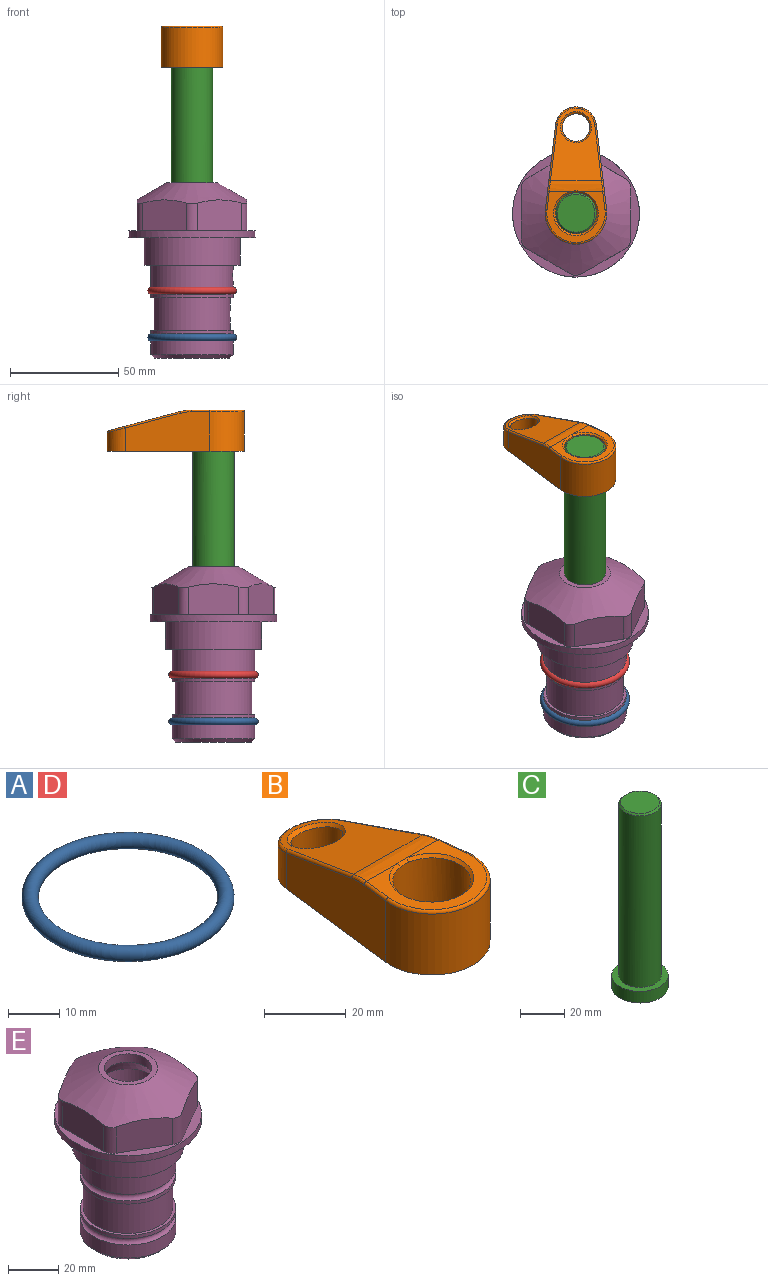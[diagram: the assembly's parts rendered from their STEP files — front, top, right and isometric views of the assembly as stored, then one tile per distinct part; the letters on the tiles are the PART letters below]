
ASSEMBLY  parts=5 mates=4
PART A: 1 faces, bbox 44.7x44.7x3.2 mm
  f0: torus R=19.05mm, axis (0,0,1), area 1193.9mm2
PART B: 31 faces, bbox 31.7x65.5x19.8 mm
  f0: plane 39.12x18.26mm, normal (0.99,0.12,0), area 612.2mm2, adj f1,f4,f7,f11,f13,f15
  f1: cylinder r=9.53mm len=18.91mm, axis (0,0,-1), area 296.1mm2, adj f0,f2,f7,f17
  f2: plane 39.12x18.26mm, normal (-0.99,0.12,0), area 612.2mm2, adj f1,f4,f7,f12,f14,f16
  f3: cylinder r=6.35mm len=12.7mm, axis (0,0,-1), area 362.4mm2, adj f7,f18
  f4: cylinder r=14.29mm len=28.58mm, axis (0,0,-1), area 882.2mm2, adj f0,f2,f7,f10
  f5: cylinder r=9.53mm len=19.05mm, axis (0,0,-1), area 1092.6mm2, adj f7,f19,f20
  f6: plane 26.99x23.69mm, normal (0,0,1), area 216.2mm2, adj f9,f10,f11,f12,f19
  f7: plane 63.5x28.58mm, normal (0,0,-1), area 661.8mm2, adj f0,f1,f2,f3,f4,f5,f22,f23
  f8: plane 33.52x23.6mm, normal (0,0.26,0.97), area 486mm2, adj f9,f15,f16,f17,f18
  f9: cylinder r=19.05mm len=24.72mm, axis (1,0,0), area 120.4mm2, adj f6,f8,f13,f14,f20
  f10: torus R=13.49mm, axis (0,0,1), area 59mm2, adj f4,f6,f11,f12
  f11: cylinder r=0.79mm len=8.67mm, axis (0.12,-0.99,0), area 10.8mm2, adj f0,f6,f10,f13
  f12: cylinder r=0.79mm len=8.67mm, axis (0.12,0.99,0), area 10.8mm2, adj f2,f6,f10,f14
  f13: bspline ~4.95x1.42mm, area 6.1mm2, adj f0,f9,f11,f15
  f14: bspline ~4.95x1.42mm, area 6.1mm2, adj f2,f9,f12,f16
  f15: cylinder r=0.79mm len=25.95mm, axis (0.12,-0.96,0.26), area 32.9mm2, adj f0,f8,f13,f17
  f16: cylinder r=0.79mm len=25.95mm, axis (0.12,0.96,-0.26), area 32.9mm2, adj f2,f8,f14,f17
  f17: bspline ~18.91x8.38mm, area 30mm2, adj f1,f8,f15,f16
  f18: bspline ~14.29x14.29mm, area 48.3mm2, adj f3,f8
  f19: cone r=9.53mm half-angle=45deg, axis (0,0,1), area 66.5mm2, adj f5,f6,f20
  f20: bspline ~3.22x0.96mm, area 3.5mm2, adj f5,f9,f19
  f21: plane 2.75x2.72mm, normal (0,0,-1), area 2.9mm2, adj f23,f25,f28
  f22: plane 23.05x15.88mm, normal (-0.99,-0.12,0), area 323.6mm2, adj f7,f25,f26,f27,f28,f29
  f23: plane 23.05x15.88mm, normal (0.99,-0.12,0), area 323.6mm2, adj f7,f21,f25,f27,f28,f30
  f24: cylinder r=9.53mm len=10.69mm, axis (0,0,-1), area 114.7mm2, adj f7,f27,f29,f30
  f25: cylinder r=12.7mm len=20.59mm, axis (0,0,-1), area 381.1mm2, adj f7,f21,f22,f23,f26,f28
  f26: plane 2.75x2.72mm, normal (0,0,-1), area 2.9mm2, adj f22,f25,f28
  f27: plane 19.72x18.37mm, normal (0,-0.26,-0.97), area 291.8mm2, adj f22,f23,f24,f28,f29,f30
  f28: cylinder r=15.88mm len=19.92mm, axis (1,0,0), area 54.8mm2, adj f21,f22,f23,f25,f26,f27
  f29: cylinder r=1.59mm len=11mm, axis (0,0,-1), area 34.7mm2, adj f7,f22,f24,f27
  f30: cylinder r=1.59mm len=11mm, axis (0,0,-1), area 34.7mm2, adj f7,f23,f24,f27
PART C: 6 faces, bbox 25.4x25.4x101.6 mm
  f0: plane 17.46x17.46mm, normal (0,0,1), area 239.5mm2, adj f5
  f1: plane 25.4x25.4mm, normal (0,0,-1), area 506.7mm2, adj f2
  f2: cylinder r=12.7mm len=25.4mm, axis (0,0,1), area 506.7mm2, adj f1,f3
  f3: plane 25.4x25.4mm, normal (0,0,1), area 221.7mm2, adj f2,f4
  f4: cylinder r=9.53mm len=94.46mm, axis (0,0,1), area 5653mm2, adj f3,f5
  f5: cone r=8.73mm half-angle=45deg, axis (0,0,-1), area 64.4mm2, adj f0,f4
PART D: same geometry as A
PART E: 36 faces, bbox 58.7x58.7x81 mm
  f0: cylinder r=17.78mm len=35.56mm, axis (0,0,1), area 1670.8mm2, adj f23,f24,f31
  f1: cylinder r=19.05mm len=38.1mm, axis (0,0,1), area 1191.9mm2, adj f26,f27,f30
  f2: plane 58.66x58.66mm, normal (0,0,-1), area 1150.6mm2, adj f3,f28
  f3: cylinder r=29.33mm len=58.66mm, axis (0,0,-1), area 585.1mm2, adj f2,f4
  f4: plane 58.66x58.66mm, normal (0,0,1), area 475.9mm2, adj f3,f5,f6,f7,f8,f9,f10,f11
  f5: plane 20.32x14.34mm, normal (-0.5,0.87,0), area 324.4mm2, adj f4,f15,f16,f17
  f6: plane 20.32x14.34mm, normal (0.5,0.87,0), area 324.4mm2, adj f4,f14,f15,f17
  f7: plane 23.48x14.34mm, normal (1,0,0), area 324.4mm2, adj f4,f13,f14,f17
  f8: plane 20.32x14.34mm, normal (0.5,-0.87,0), area 324.4mm2, adj f4,f12,f13,f17
  f9: plane 20.32x14.34mm, normal (-0.5,-0.87,0), area 324.4mm2, adj f4,f11,f12,f17
  f10: plane 23.48x14.34mm, normal (-1,0,0), area 324.4mm2, adj f4,f11,f16,f17
  f11: cylinder r=5.08mm len=12.85mm, axis (0,0,-1), area 67.2mm2, adj f4,f9,f10,f17
  f12: cylinder r=5.08mm len=12.85mm, axis (0,0,-1), area 67.2mm2, adj f4,f8,f9,f17
  f13: cylinder r=5.08mm len=12.85mm, axis (0,0,-1), area 67.2mm2, adj f4,f7,f8,f17
  f14: cylinder r=5.08mm len=12.85mm, axis (0,0,-1), area 67.2mm2, adj f4,f6,f7,f17
  f15: cylinder r=5.08mm len=12.85mm, axis (0,0,-1), area 67.2mm2, adj f4,f5,f6,f17
  f16: cylinder r=5.08mm len=12.85mm, axis (0,0,-1), area 67.2mm2, adj f4,f5,f10,f17
  f17: cone r=11.73mm half-angle=60deg, axis (0,0,-1), area 2071.8mm2, adj f5,f6,f7,f8,f9,f10,f11,f12
  f18: plane 23.46x23.46mm, normal (0,0,1), area 147.4mm2, adj f17,f35
  f19: plane 34.93x34.93mm, normal (0,0,-1), area 958mm2, adj f29
  f20: cylinder r=19.05mm len=38.1mm, axis (0,0,1), area 760.1mm2, adj f21,f29
  f21: torus R=19.05mm, axis (0,0,1), area 565.3mm2, adj f20,f22
  f22: cylinder r=19.05mm len=38.1mm, axis (0,0,1), area 190mm2, adj f21,f23
  f23: plane 38.1x38.1mm, normal (0,0,1), area 146.9mm2, adj f0,f22
  f24: plane 38.1x38.1mm, normal (0,0,-1), area 146.9mm2, adj f0,f25
  f25: cylinder r=19.05mm len=38.1mm, axis (0,0,1), area 190mm2, adj f24,f26
  f26: torus R=19.05mm, axis (0,0,1), area 565.3mm2, adj f1,f25
  f27: plane 44.45x44.45mm, normal (0,0,-1), area 411.7mm2, adj f1,f28
  f28: cylinder r=22.23mm len=44.45mm, axis (0,0,1), area 1773.5mm2, adj f2,f27
  f29: cone r=19.05mm half-angle=45deg, axis (0,0,1), area 257.5mm2, adj f19,f20
  f30: cylinder r=3.17mm len=6.75mm, axis (-1,0,0), area 128mm2, adj f1,f33
  f31: cylinder r=3.17mm len=6.35mm, axis (-1,0,0), area 102.5mm2, adj f0,f33
  f32: plane 25.4x25.4mm, normal (0,0,1), area 506.7mm2, adj f33
  f33: cylinder r=12.7mm len=66.42mm, axis (0,0,-1), area 5236.2mm2, adj f30,f31,f32,f34
  f34: cone r=9.53mm half-angle=30deg, axis (0,0,-1), area 443.4mm2, adj f33,f35
  f35: cylinder r=9.53mm len=19.05mm, axis (0,0,-1), area 240.9mm2, adj f18,f34
PLACE A t=(-82.44,-6.87,-35.4)mm
PLACE B t=(-82.44,-6.87,20.57)mm
PLACE C t=(-82.44,-6.87,19.77)mm
PLACE D t=(-82.44,-6.87,-13.81)mm
PLACE E t=(-82.44,-6.87,-13.81)mm
MATE fastened B.f4 <-> C.f2  axis (0,0,-1) through (-82.44,-6.87,83.27)mm
MATE cylindrical C.f2 <-> E.f0  axis (0,0,-1) through (-82.44,-6.87,-18.33)mm
MATE fastened E.f0 <-> D.f0  axis (0,0,1) through (-82.44,-6.87,-38.32)mm
MATE fastened E.f0 <-> A.f0  axis (0,0,1) through (-82.44,-6.87,-59.91)mm
